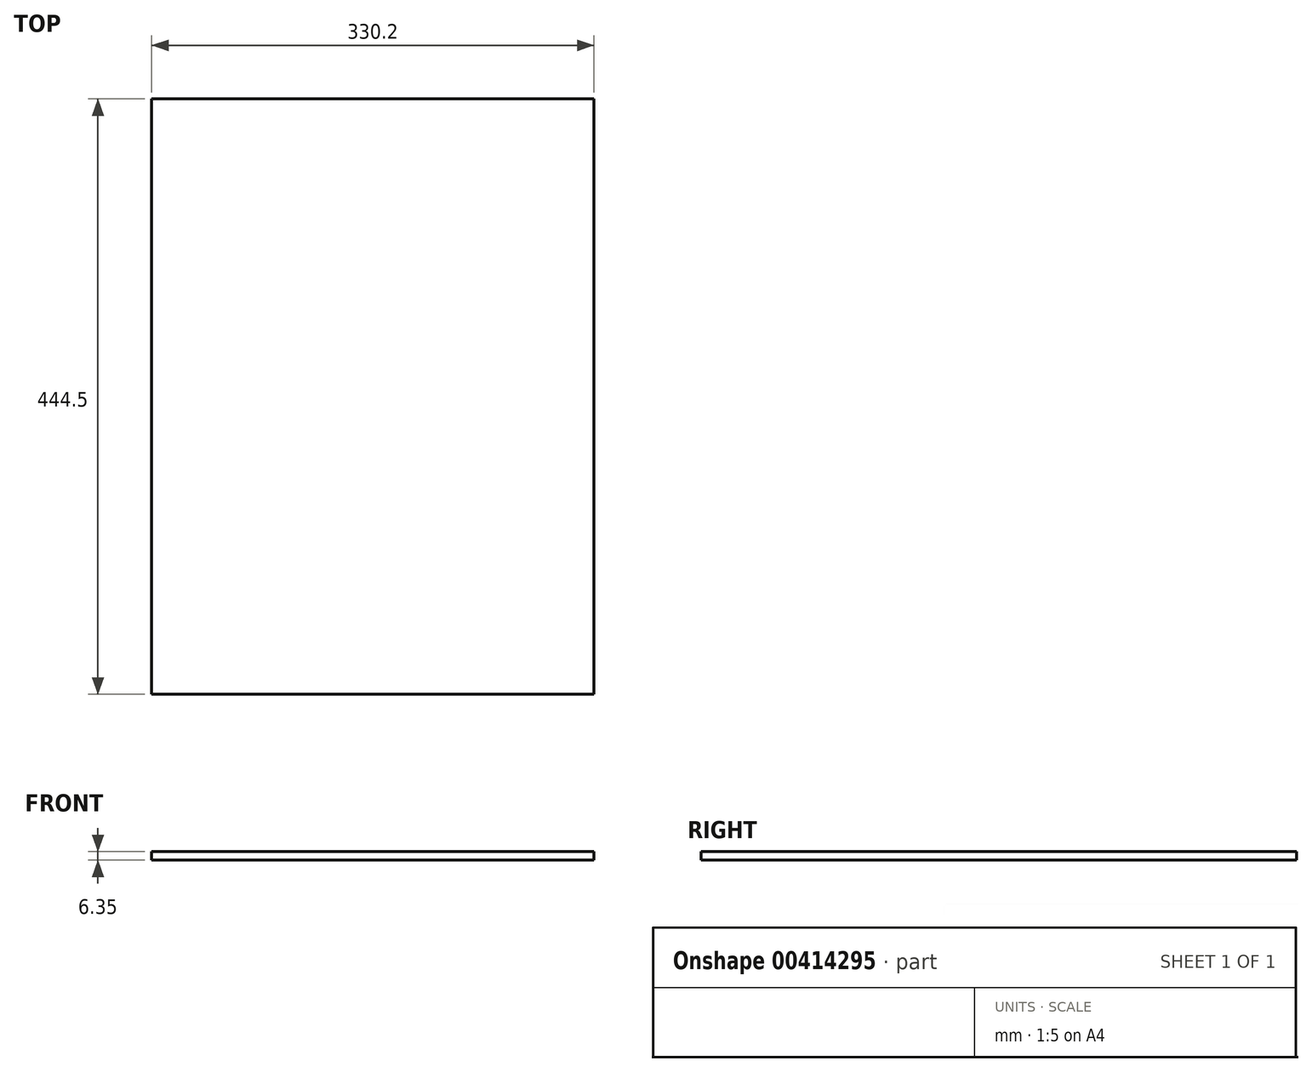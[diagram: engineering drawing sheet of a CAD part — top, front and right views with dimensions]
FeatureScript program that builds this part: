
annotation { "Feature Type Name" : "Feature", "Feature Type Description" : "" }
export const myFeature = defineFeature(function(context is Context, id is Id, definition is map)
    precondition{}
    {
        {
            var Q0;
            Q0=qCreatedBy(makeId("Front.planeOp"),FACE);
            var sketch = newSketch(context, id + "F0", { "sketchPlane" : qUnion([Q0])});
            skLineSegment(sketch, "E0.bottom", {"start": v(0, 0) * mm, "end": v(-330.2, 0) * mm});
            skLineSegment(sketch, "E0.top", {"start": v(0, 6.35) * mm, "end": v(-330.2, 6.35) * mm});
            skLineSegment(sketch, "E0.left", {"start": v(0, 0) * mm, "end": v(0, 6.35) * mm});
            skLineSegment(sketch, "E0.right", {"start": v(-330.2, 0) * mm, "end": v(-330.2, 6.35) * mm});
            skSolve(sketch);
        }
        {
            var Q0;
            Q0=qSketchRegion(id+"F0",true);
            extrude(context, id + "F1", {"entities" : qUnion([Q0]), "depth" : 444.5 * mm});
        }
    });
